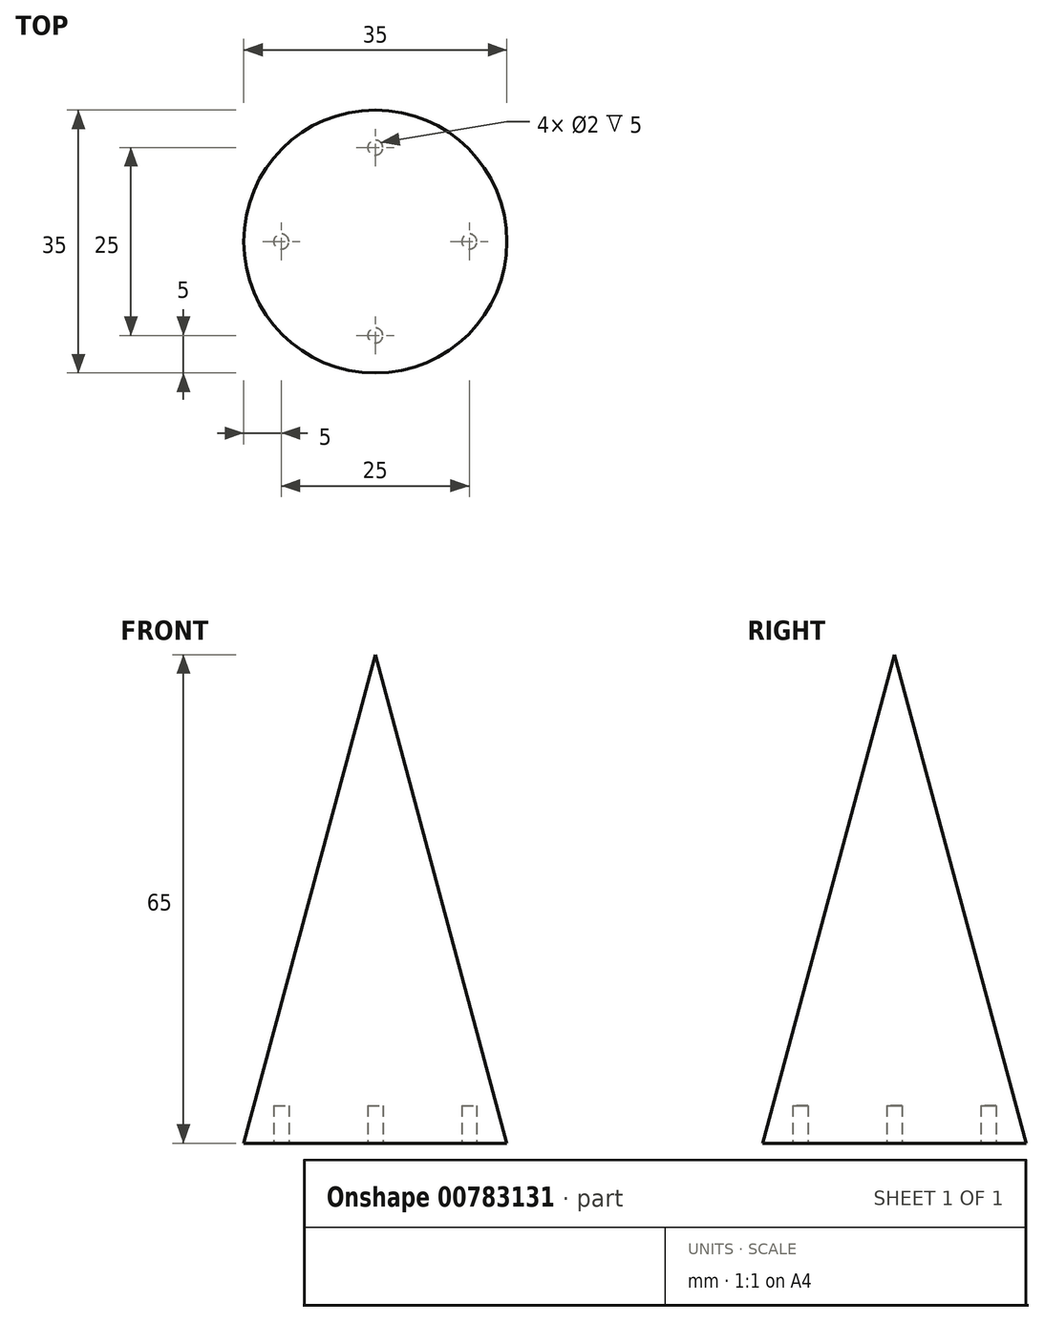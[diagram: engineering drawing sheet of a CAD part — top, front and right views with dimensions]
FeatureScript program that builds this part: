
annotation { "Feature Type Name" : "Feature", "Feature Type Description" : "" }
export const myFeature = defineFeature(function(context is Context, id is Id, definition is map)
    precondition{}
    {
        {
            var Q0;
            Q0=qCreatedBy(makeId("Front.planeOp"),FACE);
            var sketch = newSketch(context, id + "F0", { "sketchPlane" : qUnion([Q0])});
            skLineSegment(sketch, "E0", {"start": v(0, 0) * mm, "end": v(0, 65) * mm});
            skLineSegment(sketch, "E1", {"start": v(0, 65) * mm, "end": v(-17.5, 0) * mm});
            skLineSegment(sketch, "E2", {"start": v(-17.5, 0) * mm, "end": v(0, 0) * mm});
            skSolve(sketch);
        }
        {
            var Q0;
            Q0=makeQuery(id+"F0.imprint","IMPRINT",FACE,{"disambiguationData":[TD([[makeQuery(id+"F0.imprint","IMPRINT",EDGE,{"derivedFrom":sQuery(id+"F0.wireOp",EDGE,"E0")}),1.0]])]});
            var Q1;
            Q1=sQuery(id+"F0.wireOp",EDGE,"E0");
            revolve(context, id + "F1", {"surfaceOperationType" : NewSurfaceOperationType.NEW, "entities" : qUnion([Q0]), "axis" : qUnion([Q1]), "revolveType" : RevolveType.FULL});
        }
        {
            var Q0;
            Q0=makeQuery(id+"F1.opRevolve","SWEPT_FACE",FACE,{"disambiguationData":[OSD([sQuery(id+"F0.wireOp",EDGE,"E2")])]});
            var sketch = newSketch(context, id + "F2", { "sketchPlane" : qUnion([Q0])});
            skCircle(sketch, "E3", {"center": v(-12.5, 0) * mm, "radius": 1 * mm});
            skCircle(sketch, "E4", {"center": v(12.5, 0) * mm, "radius": 1 * mm});
            skCircle(sketch, "E5", {"center": v(0, -12.5) * mm, "radius": 1 * mm});
            skCircle(sketch, "E6", {"center": v(0, 12.5) * mm, "radius": 1 * mm});
            skSolve(sketch);
        }
        {
            var Q0;
            Q0=makeQuery(id+"F2.imprint","IMPRINT",FACE,{"disambiguationData":[TD([[makeQuery(id+"F2.imprint","IMPRINT",EDGE,{"derivedFrom":sQuery(id+"F2.wireOp",EDGE,"E5")}),1.0]])]});
            var Q1;
            Q1=makeQuery(id+"F2.imprint","IMPRINT",FACE,{"disambiguationData":[TD([[makeQuery(id+"F2.imprint","IMPRINT",EDGE,{"derivedFrom":sQuery(id+"F2.wireOp",EDGE,"E3")}),1.0]])]});
            var Q2;
            Q2=makeQuery(id+"F2.imprint","IMPRINT",FACE,{"disambiguationData":[TD([[makeQuery(id+"F2.imprint","IMPRINT",EDGE,{"derivedFrom":sQuery(id+"F2.wireOp",EDGE,"E6")}),1.0]])]});
            var Q3;
            Q3=makeQuery(id+"F2.imprint","IMPRINT",FACE,{"disambiguationData":[TD([[makeQuery(id+"F2.imprint","IMPRINT",EDGE,{"derivedFrom":sQuery(id+"F2.wireOp",EDGE,"E4")}),1.0]])]});
            extrude(context, id + "F3", {"entities" : qUnion([Q0, Q1, Q2, Q3]), "operationType" : NewBodyOperationType.REMOVE, "oppositeDirection" : true, "depth" : 5 * mm, "offsetDistance" : 25 * mm});
        }
    });
